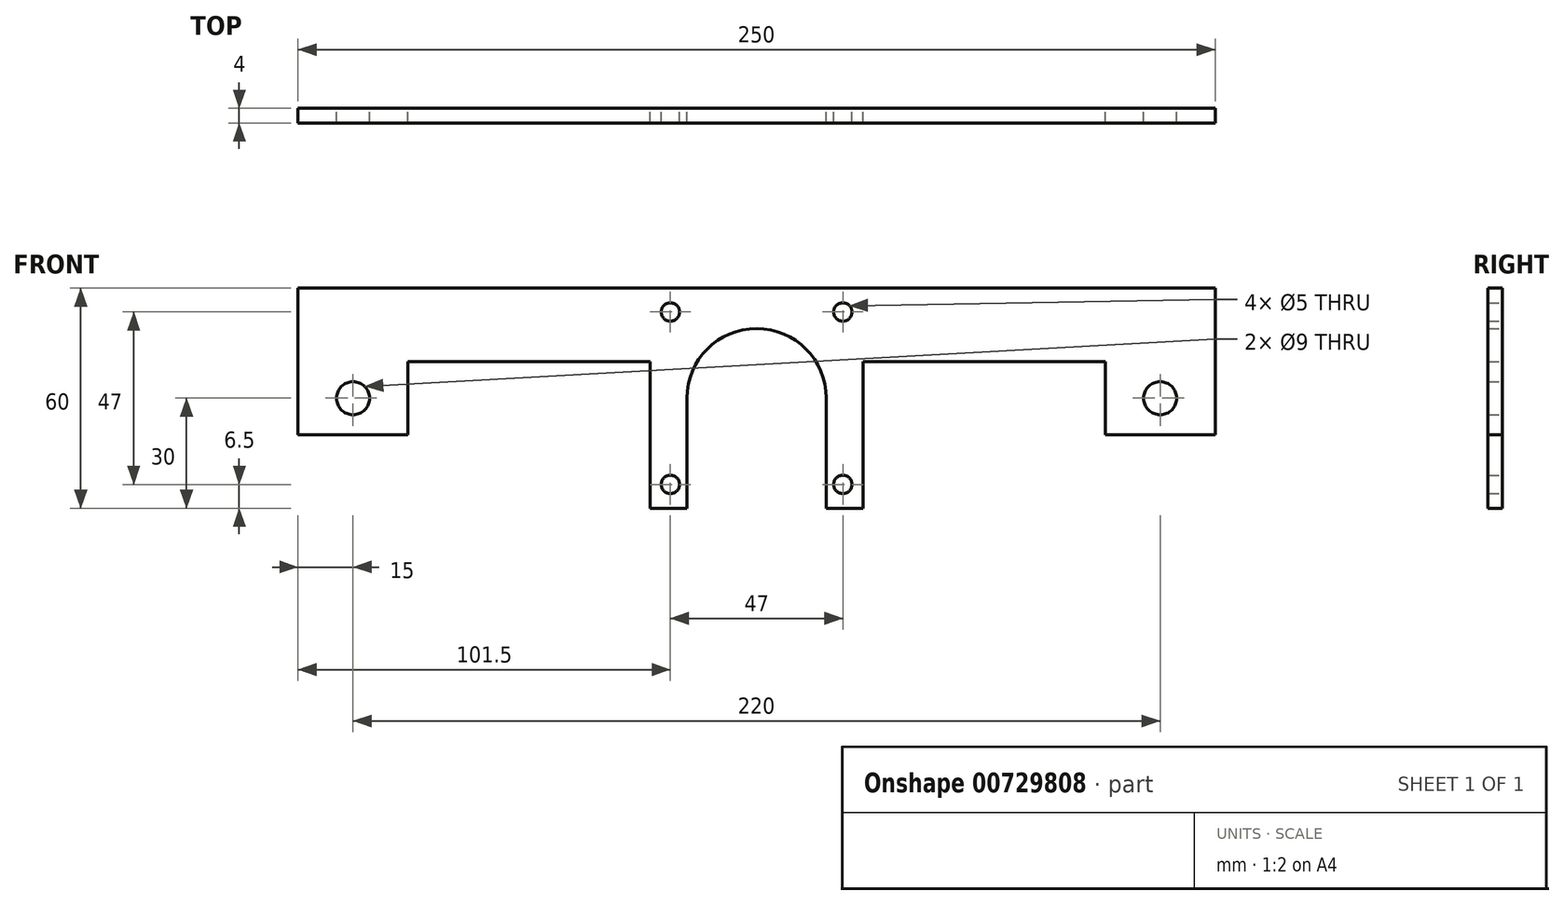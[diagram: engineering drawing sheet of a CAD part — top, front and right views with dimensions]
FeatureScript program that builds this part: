
annotation { "Feature Type Name" : "Feature", "Feature Type Description" : "" }
export const myFeature = defineFeature(function(context is Context, id is Id, definition is map)
    precondition{}
    {
        {
            var Q0;
            Q0=qCreatedBy(makeId("Front.planeOp"),FACE);
            var sketch = newSketch(context, id + "F0", { "sketchPlane" : qUnion([Q0])});
            skPoint(sketch, "E0.middle", {"position": v(0, 0) * mm});
            skLineSegment(sketch, "E1.bottom", {"start": v(23.5, 23.5) * mm, "end": v(-23.5, 23.5) * mm, "construction": true});
            skLineSegment(sketch, "E1.top", {"start": v(23.5, -23.5) * mm, "end": v(-23.5, -23.5) * mm, "construction": true});
            skLineSegment(sketch, "E1.left", {"start": v(23.5, 23.5) * mm, "end": v(23.5, -23.5) * mm, "construction": true});
            skLineSegment(sketch, "E1.right", {"start": v(-23.5, 23.5) * mm, "end": v(-23.5, -23.5) * mm, "construction": true});
            skCircle(sketch, "E2", {"center": v(-23.5, 23.5) * mm, "radius": 2.5 * mm});
            skCircle(sketch, "E3", {"center": v(23.5, 23.5) * mm, "radius": 2.5 * mm});
            skCircle(sketch, "E4", {"center": v(-23.5, -23.5) * mm, "radius": 2.5 * mm});
            skCircle(sketch, "E5", {"center": v(23.5, -23.5) * mm, "radius": 2.5 * mm});
            skArc(sketch, "E6", {"start": v(19, 0) * mm, "mid": v(0, 19) * mm, "end": v(-19, 0) * mm});
            skLineSegment(sketch, "E7", {"start": v(-19, 0) * mm, "end": v(-19, -30) * mm});
            skLineSegment(sketch, "E8", {"start": v(19, 0) * mm, "end": v(19, -30) * mm});
            skLineSegment(sketch, "E9", {"start": v(19, -30) * mm, "end": v(29, -30) * mm});
            skLineSegment(sketch, "E10", {"start": v(29, -30) * mm, "end": v(29, 10) * mm});
            skLineSegment(sketch, "E11", {"start": v(29, 10) * mm, "end": v(95, 10) * mm});
            skLineSegment(sketch, "E12", {"start": v(125, 30) * mm, "end": v(-125, 30) * mm});
            skLineSegment(sketch, "E13", {"start": v(-95, 10) * mm, "end": v(-29, 10) * mm});
            skLineSegment(sketch, "E14", {"start": v(-29, 10) * mm, "end": v(-29, -30) * mm});
            skLineSegment(sketch, "E15", {"start": v(-29, -30) * mm, "end": v(-19, -30) * mm});
            skLineSegment(sketch, "E16", {"start": v(-95, 10) * mm, "end": v(-95, -10) * mm});
            skLineSegment(sketch, "E17", {"start": v(-95, -10) * mm, "end": v(-125, -10) * mm});
            skLineSegment(sketch, "E18", {"start": v(-125, -10) * mm, "end": v(-125, 30) * mm});
            skLineSegment(sketch, "E19", {"start": v(125, 30) * mm, "end": v(125, -10) * mm});
            skLineSegment(sketch, "E20", {"start": v(125, -10) * mm, "end": v(95, -10) * mm});
            skLineSegment(sketch, "E21", {"start": v(95, -10) * mm, "end": v(95, 10) * mm});
            skLineSegment(sketch, "E22", {"start": v(-110, 0) * mm, "end": v(0, 0) * mm, "construction": true});
            skLineSegment(sketch, "E23", {"start": v(0, 0) * mm, "end": v(110, 0) * mm, "construction": true});
            skCircle(sketch, "E24", {"center": v(110, 0) * mm, "radius": 4.5 * mm});
            skCircle(sketch, "E25", {"center": v(-110, 0) * mm, "radius": 4.5 * mm});
            skSolve(sketch);
        }
        {
            var Q0;
            Q0 = qSketchRegion(id + "F0", true);
            extrude(context, id + "F1", {"entities" : qUnion([Q0]), "depth" : 4 * mm, "offsetDistance" : 25 * mm});
        }
    });
